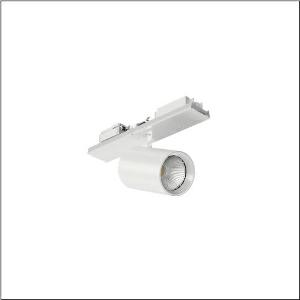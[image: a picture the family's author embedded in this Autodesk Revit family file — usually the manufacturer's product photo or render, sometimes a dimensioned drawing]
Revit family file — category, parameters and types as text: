
# Revit family: licross_r__spot_31_51sl137a45b_29a8
name_source: partatom
category: Lighting Fixtures
units: mm (PartAtom-declared; Revit-internal decimal feet)

## family parameters
Cut with Voids When Loaded = No
Host = Face
Light Source = No
Part Type = Normal
Room Calculation Point = No
Round Connector Dimension = Use Diameter
Shared = No

## types (1)
- --- (1 x LED, 5190 lm, 42.6 W, 4000K)
    Apparent Load = 43 VA
    CIE Flux Codes = 92 97 99 100 100
    Color Rendering = 90
    Color Temperature = 4000K
    Default Elevation = 1800 mm
    Description = Licross® Spot 31, directional spotlight, light control with lens, of plastic, LED rated luminous flux: 5.190lm, light colour: 940, with plug, 3-pole, with phase selection, mains connection: 220..240V, AC, 50/60Hz, of aluminium, traffic white (RAL 9016), length: 140mm, diameter: 90mm, protection rating (complete): IP20, insulation class (complete): insulation class I (protective earthing), certification: CE, packaging unit: 1 piece
    Height = 175 mm
    Lamp = 1 x LED
    Lamp Light Flux = 5190 lm
    Lamp Power = 42.6 W
    Lamp count = 1
    Length = 90 mm
    Luminous efficacy = 122 lm/W
    Manufacturer = Siteco
    ModVariant = No
    Model = 51SL137A45B
    Mounting Place = Ceiling
    Mounting Type = Pendant
    Number of Poles = 1
    OnlyDefault = Yes
    Power Factor = 1
    Product Name = Licross® Spot 31
    Product group = directional spotlight
    ProductGroupID = 905
    Protection Class = Protection class I
    Protection Degree = IP 20
    RLX_Detail_Level = 1
    RLX_Emergency_Light_Flux = 0 lm
    RLX_Emergency_Type = 0
    RLX_Emergency_Type_DB = No
    RlxData = <blob elided: 14793 chars, md5=4ed5fe60>
    Socket = socket
    Standby Power = 0 W
    System Light Flux = 5190 lm
    System Power = 43 W
    Type Comments = factory setting: luminous flux: 100 % | (ON | ON | ON) | 1050 mA
    Type Image = l_1245720.jpg
    URL = http://relux.com
    VarID = @adj_063879
    Voltage = 0 V
    Weight = 0.00 kg
    Width = 0 mm  [stored 0 ft]

note: [stored X ft] marks values corroborated as IEEE doubles in the binary element streams (Revit-internal decimal feet)

## geometry (parser evidence)
native form markers: Sweep x13
no freeform markers — native parametric forms only
